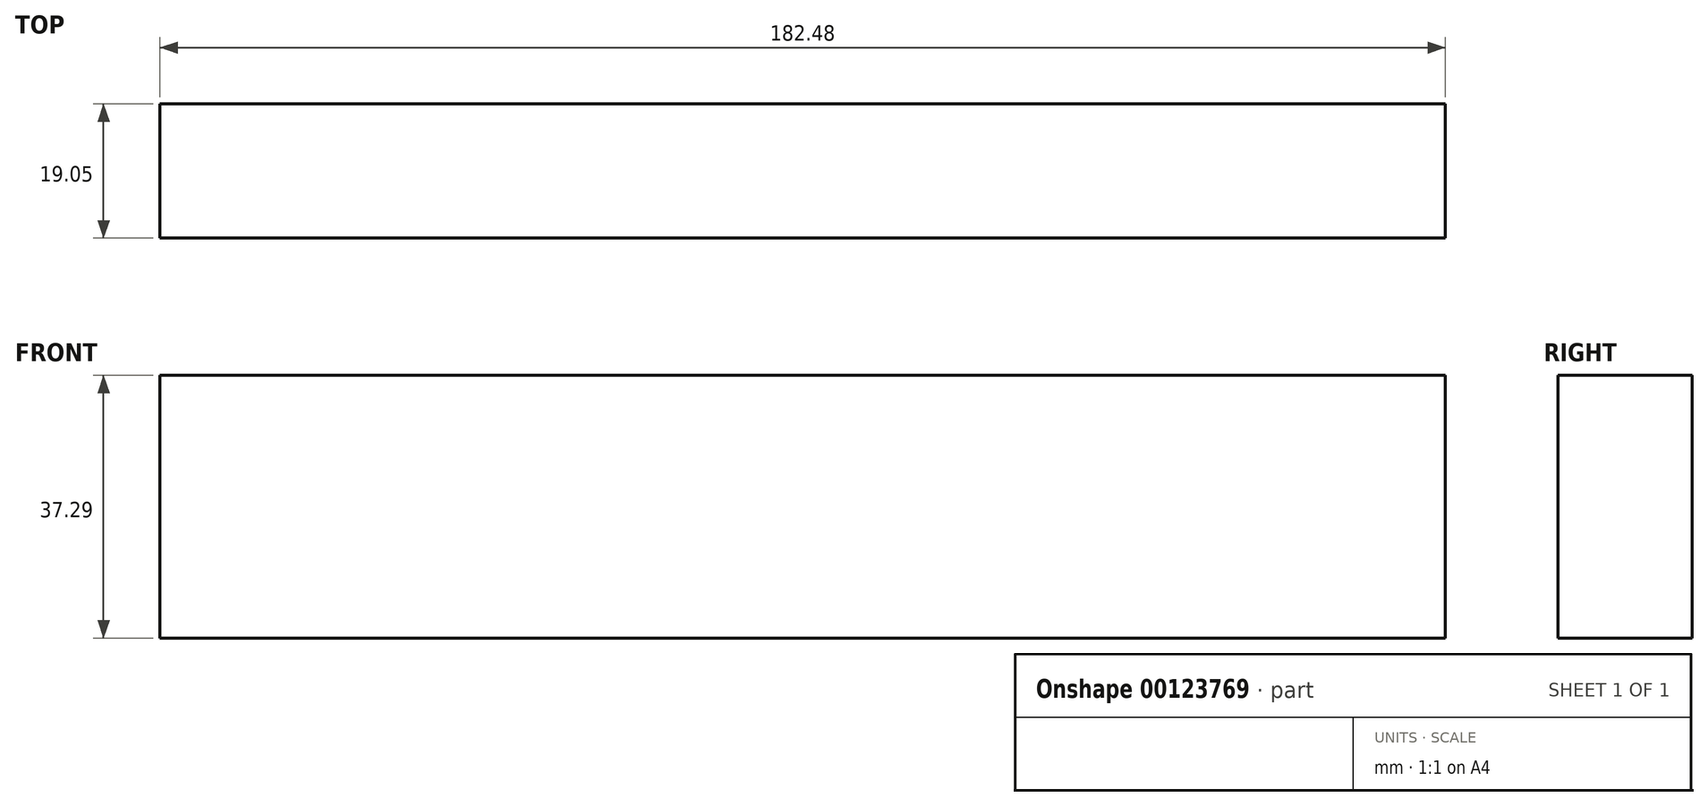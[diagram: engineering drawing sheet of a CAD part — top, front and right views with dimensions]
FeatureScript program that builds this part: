
annotation { "Feature Type Name" : "Feature", "Feature Type Description" : "" }
export const myFeature = defineFeature(function(context is Context, id is Id, definition is map)
    precondition{}
    {
        {
            var Q0;
            Q0=qCreatedBy(makeId("Front.planeOp"),FACE);
            var sketch = newSketch(context, id + "F0", { "sketchPlane" : qUnion([Q0])});
            skLineSegment(sketch, "E0.bottom", {"start": v(72.95, -31.14) * mm, "end": v(-109.53, -31.14) * mm});
            skLineSegment(sketch, "E0.top", {"start": v(72.95, 6.15) * mm, "end": v(-109.53, 6.15) * mm});
            skLineSegment(sketch, "E0.left", {"start": v(72.95, -31.14) * mm, "end": v(72.95, 6.15) * mm});
            skLineSegment(sketch, "E0.right", {"start": v(-109.53, -31.14) * mm, "end": v(-109.53, 6.15) * mm});
            skSolve(sketch);
        }
        {
            var Q0;
            Q0=makeQuery(id+"F0.imprint","IMPRINT",FACE,{"disambiguationData":[TD([[makeQuery(id+"F0.imprint","IMPRINT",EDGE,{"derivedFrom":sQuery(id+"F0.wireOp",EDGE,"E0.bottom")}),-1.0]])]});
            extrude(context, id + "F1", {"entities" : qUnion([Q0]), "depth" : 19.05 * mm});
        }
    });
